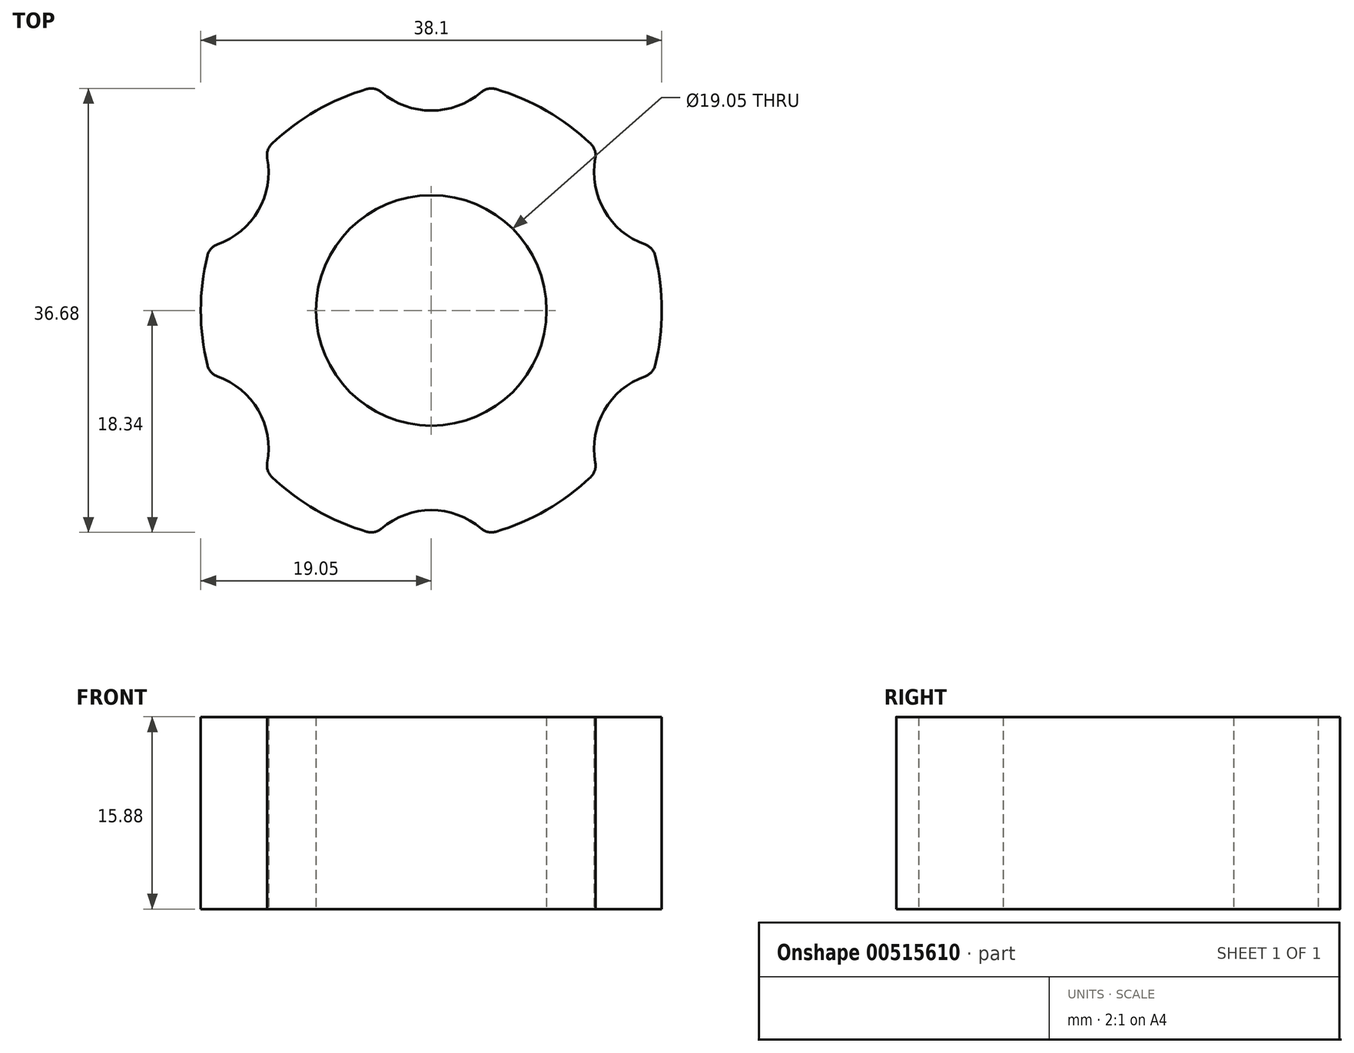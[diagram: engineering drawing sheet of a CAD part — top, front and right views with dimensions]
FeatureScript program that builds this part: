
annotation { "Feature Type Name" : "Feature", "Feature Type Description" : "" }
export const myFeature = defineFeature(function(context is Context, id is Id, definition is map)
    precondition{}
    {
        {
            var Q0;
            Q0=qCreatedBy(makeId("Top.planeOp"),FACE);
            var sketch = newSketch(context, id + "F0", { "sketchPlane" : qUnion([Q0])});
            skArc(sketch, "E0", {"start": v(-4.6, 18.49) * mm, "mid": v(-9.52, 16.5) * mm, "end": v(-13.7, 13.23) * mm});
            skCircle(sketch, "E1", {"center": v(0, 0) * mm, "radius": 9.53 * mm});
            skCircle(sketch, "E2", {"center": v(0, 0) * mm, "radius": 22.86 * mm, "construction": true});
            skPoint(sketch, "E3", {"position": v(0, 22.86) * mm});
            skArc(sketch, "E4", {"start": v(-4.6, 18.49) * mm, "mid": v(0, 16.51) * mm, "end": v(4.6, 18.49) * mm});
            skArc(sketch, "E5.1.0", {"start": v(-18.31, 5.26) * mm, "mid": v(-14.3, 8.25) * mm, "end": v(-13.7, 13.23) * mm});
            skArc(sketch, "E5.2.0", {"start": v(-13.7, -13.23) * mm, "mid": v(-14.3, -8.25) * mm, "end": v(-18.31, -5.26) * mm});
            skArc(sketch, "E5.3.0", {"start": v(4.6, -18.49) * mm, "mid": v(0, -16.5) * mm, "end": v(-4.6, -18.49) * mm});
            skArc(sketch, "E5.4.0", {"start": v(18.31, -5.26) * mm, "mid": v(14.3, -8.26) * mm, "end": v(13.7, -13.23) * mm});
            skArc(sketch, "E5.5.0", {"start": v(13.7, 13.23) * mm, "mid": v(14.3, 8.26) * mm, "end": v(18.31, 5.26) * mm});
            skArc(sketch, "E6.trimOffspring", {"start": v(-18.31, 5.26) * mm, "mid": v(-19.05, 0) * mm, "end": v(-18.31, -5.26) * mm});
            skArc(sketch, "E7.trimOffspring", {"start": v(13.7, 13.23) * mm, "mid": v(9.53, 16.5) * mm, "end": v(4.6, 18.49) * mm});
            skArc(sketch, "E8.trimOffspring", {"start": v(18.31, -5.26) * mm, "mid": v(19.05, 0) * mm, "end": v(18.31, 5.26) * mm});
            skArc(sketch, "E9.trimOffspring", {"start": v(4.6, -18.49) * mm, "mid": v(9.52, -16.5) * mm, "end": v(13.7, -13.23) * mm});
            skArc(sketch, "E10.trimOffspring", {"start": v(-13.7, -13.23) * mm, "mid": v(-9.53, -16.5) * mm, "end": v(-4.6, -18.49) * mm});
            skSolve(sketch);
        }
        {
            var Q0;
            Q0 = qSketchRegion(id + "F0", true);
            extrude(context, id + "F1", {"entities" : qUnion([Q0]), "depth" : 15.88 * mm, "offsetDistance" : 25.4 * mm});
        }
        {
            var Q0;
            Q0=makeQuery(id+"F1.opExtrude","SWEPT_EDGE",EDGE,{"disambiguationData":[OSD([sQuery(id+"F0.wireOp",EDGE,"E5.4.0"),sQuery(id+"F0.wireOp",EDGE,"E9.trimOffspring")])]});
            var Q1;
            Q1=makeQuery(id+"F1.opExtrude","SWEPT_EDGE",EDGE,{"disambiguationData":[OSD([sQuery(id+"F0.wireOp",EDGE,"E5.3.0"),sQuery(id+"F0.wireOp",EDGE,"E9.trimOffspring")])]});
            var Q2;
            Q2=makeQuery(id+"F1.opExtrude","SWEPT_EDGE",EDGE,{"disambiguationData":[OSD([sQuery(id+"F0.wireOp",EDGE,"E5.4.0"),sQuery(id+"F0.wireOp",EDGE,"E8.trimOffspring")])]});
            var Q3;
            Q3=makeQuery(id+"F1.opExtrude","SWEPT_EDGE",EDGE,{"disambiguationData":[OSD([sQuery(id+"F0.wireOp",EDGE,"E5.5.0"),sQuery(id+"F0.wireOp",EDGE,"E8.trimOffspring")])]});
            var Q4;
            Q4=makeQuery(id+"F1.opExtrude","SWEPT_EDGE",EDGE,{"disambiguationData":[OSD([sQuery(id+"F0.wireOp",EDGE,"E5.5.0"),sQuery(id+"F0.wireOp",EDGE,"E7.trimOffspring")])]});
            var Q5;
            Q5=makeQuery(id+"F1.opExtrude","SWEPT_EDGE",EDGE,{"disambiguationData":[OSD([sQuery(id+"F0.wireOp",EDGE,"E4"),sQuery(id+"F0.wireOp",EDGE,"E7.trimOffspring")])]});
            var Q6;
            Q6=makeQuery(id+"F1.opExtrude","SWEPT_EDGE",EDGE,{"disambiguationData":[OSD([sQuery(id+"F0.wireOp",EDGE,"E0"),sQuery(id+"F0.wireOp",EDGE,"E4")])]});
            var Q7;
            Q7=makeQuery(id+"F1.opExtrude","SWEPT_EDGE",EDGE,{"disambiguationData":[OSD([sQuery(id+"F0.wireOp",EDGE,"E0"),sQuery(id+"F0.wireOp",EDGE,"E5.1.0")])]});
            var Q8;
            Q8=makeQuery(id+"F1.opExtrude","SWEPT_EDGE",EDGE,{"disambiguationData":[OSD([sQuery(id+"F0.wireOp",EDGE,"E5.1.0"),sQuery(id+"F0.wireOp",EDGE,"E6.trimOffspring")])]});
            var Q9;
            Q9=makeQuery(id+"F1.opExtrude","SWEPT_EDGE",EDGE,{"disambiguationData":[OSD([sQuery(id+"F0.wireOp",EDGE,"E5.2.0"),sQuery(id+"F0.wireOp",EDGE,"E6.trimOffspring")])]});
            var Q10;
            Q10=makeQuery(id+"F1.opExtrude","SWEPT_EDGE",EDGE,{"disambiguationData":[OSD([sQuery(id+"F0.wireOp",EDGE,"E5.2.0"),sQuery(id+"F0.wireOp",EDGE,"E10.trimOffspring")])]});
            var Q11;
            Q11=makeQuery(id+"F1.opExtrude","SWEPT_EDGE",EDGE,{"disambiguationData":[OSD([sQuery(id+"F0.wireOp",EDGE,"E5.3.0"),sQuery(id+"F0.wireOp",EDGE,"E10.trimOffspring")])]});
            fillet(context, id + "F2", {"entities" : qUnion([Q0, Q1, Q2, Q3, Q4, Q5, Q6, Q7, Q8, Q9, Q10, Q11]), "radius" : 1.27 * mm, "tangentPropagation" : true, "allowEdgeOverflow" : false});
        }
    });
